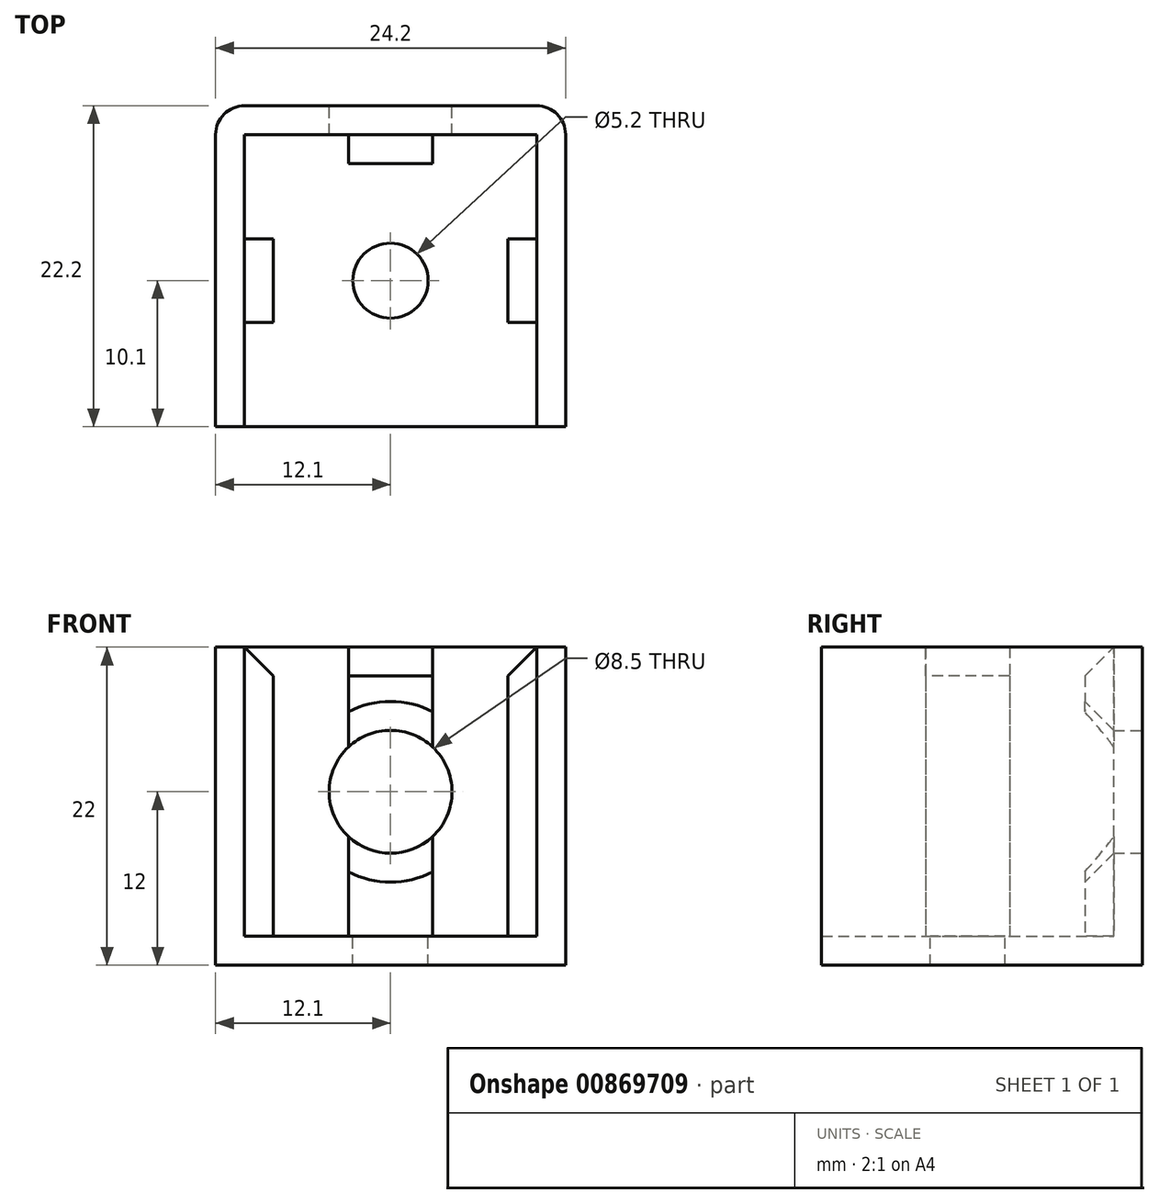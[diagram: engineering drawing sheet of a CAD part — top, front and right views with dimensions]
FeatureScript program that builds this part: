
annotation { "Feature Type Name" : "Feature", "Feature Type Description" : "" }
export const myFeature = defineFeature(function(context is Context, id is Id, definition is map)
    precondition{}
    {
        {
            var Q0;
            Q0=qCreatedBy(makeId("Top.planeOp"),FACE);
            var sketch = newSketch(context, id + "F0", { "sketchPlane" : qUnion([Q0])});
            skLineSegment(sketch, "E0.bottom", {"start": v(10.1, 10.1) * mm, "end": v(-10.1, 10.1) * mm});
            skLineSegment(sketch, "E0.top", {"start": v(10.1, -10.1) * mm, "end": v(-10.1, -10.1) * mm});
            skLineSegment(sketch, "E0.left", {"start": v(10.1, 10.1) * mm, "end": v(10.1, -10.1) * mm});
            skLineSegment(sketch, "E0.right", {"start": v(-10.1, 10.1) * mm, "end": v(-10.1, -10.1) * mm});
            skPoint(sketch, "E0.middle", {"position": v(0, 0) * mm});
            skSolve(sketch);
        }
        {
            var Q0;
            Q0=qCreatedBy(makeId("Top.planeOp"),FACE);
            var sketch = newSketch(context, id + "F1", { "sketchPlane" : qUnion([Q0])});
            skLineSegment(sketch, "E1.bottom", {"start": v(-12.1, 10.1) * mm, "end": v(12.1, 10.1) * mm});
            skLineSegment(sketch, "E1.top", {"start": v(-12.1, 12.1) * mm, "end": v(12.1, 12.1) * mm});
            skLineSegment(sketch, "E1.left", {"start": v(-12.1, 10.1) * mm, "end": v(-12.1, 12.1) * mm});
            skLineSegment(sketch, "E1.right", {"start": v(12.1, 10.1) * mm, "end": v(12.1, 12.1) * mm});
            skLineSegment(sketch, "E2.bottom", {"start": v(-2.9, 10.1) * mm, "end": v(2.9, 10.1) * mm});
            skLineSegment(sketch, "E2.top", {"start": v(-2.9, 8.1) * mm, "end": v(2.9, 8.1) * mm});
            skLineSegment(sketch, "E2.left", {"start": v(-2.9, 10.1) * mm, "end": v(-2.9, 8.1) * mm});
            skLineSegment(sketch, "E2.right", {"start": v(2.9, 10.1) * mm, "end": v(2.9, 8.1) * mm});
            skLineSegment(sketch, "E3", {"start": v(0, 0) * mm, "end": v(0, 8.1) * mm, "construction": true});
            skLineSegment(sketch, "E4", {"start": v(0, 8.1) * mm, "end": v(0, 10.1) * mm, "construction": true});
            skSolve(sketch);
        }
        {
            var Q0;
            Q0=qSketchRegion(id+"F1",true);
            extrude(context, id + "F2", {"entities" : qUnion([Q0]), "depth" : 20 * mm, "offsetDistance" : 25 * mm});
        }
        {
            var Q0;
            Q0=qCreatedBy(makeId("Front.planeOp"),FACE);
            var sketch = newSketch(context, id + "F3", { "sketchPlane" : qUnion([Q0])});
            skLineSegment(sketch, "E5", {"start": v(0, 0) * mm, "end": v(0, 26.41) * mm, "construction": true});
            skSolve(sketch);
        }
        {
            var Q0;
            Q0=makeQuery(id+"F2.opExtrude","SWEPT_BODY",BODY,{"disambiguationData":[OSD([sQuery(id+"F1.wireOp",EDGE,"E1.bottom"),sQuery(id+"F1.wireOp",EDGE,"E1.top"),sQuery(id+"F1.wireOp",EDGE,"E1.left"),sQuery(id+"F1.wireOp",EDGE,"E1.right"),sQuery(id+"F1.wireOp",EDGE,"E2.top"),sQuery(id+"F1.wireOp",EDGE,"E2.left"),sQuery(id+"F1.wireOp",EDGE,"E2.right")])]});
            var Q1;
            Q1=sQuery(id+"F3.wireOp",EDGE,"E5");
            circularPattern(context, id + "F4", {"operationType" : NewBodyOperationType.ADD, "entities" : qUnion([Q0]), "axis" : qUnion([Q1]), "angle" : 360 * degree, "instanceCount" : 4, "equalSpace" : true});
        }
        {
            var Q0;
            Q0=makeQuery(id+"F2.opExtrude","SWEPT_FACE",FACE,{"disambiguationData":[OSD([sQuery(id+"F1.wireOp",EDGE,"E1.top")])]});
            var sketch = newSketch(context, id + "F5", { "sketchPlane" : qUnion([Q0])});
            skCircle(sketch, "E6", {"center": v(0, 10) * mm, "radius": 4.25 * mm});
            skSolve(sketch);
        }
        {
            var Q0;
            Q0=qSketchRegion(id+"F5",true);
            extrude(context, id + "F6", {"entities" : qUnion([Q0]), "operationType" : NewBodyOperationType.REMOVE, "endBound" : BoundingType.THROUGH_ALL, "oppositeDirection" : true, "depth" : 25 * mm, "offsetDistance" : 25 * mm});
        }
        {
            var Q0;
            {var subQ0=makeQuery(id+"F2.opExtrude","CAP_FACE",FACE,{"disambiguationData":[OSD([sQuery(id+"F1.wireOp",EDGE,"E1.bottom"),sQuery(id+"F1.wireOp",EDGE,"E1.top"),sQuery(id+"F1.wireOp",EDGE,"E1.left"),sQuery(id+"F1.wireOp",EDGE,"E1.right"),sQuery(id+"F1.wireOp",EDGE,"E2.top"),sQuery(id+"F1.wireOp",EDGE,"E2.left"),sQuery(id+"F1.wireOp",EDGE,"E2.right")])],"isStart":false});Q0=makeQuery(id+"F4.boolean.opBoolean","MERGE",FACE,{"derivedFrom":[subQ0,makeQuery(id+"F4.opPattern","COPY",FACE,{"derivedFrom":subQ0,"instanceName":"1"}),makeQuery(id+"F4.opPattern","COPY",FACE,{"derivedFrom":subQ0,"instanceName":"2"}),makeQuery(id+"F4.opPattern","COPY",FACE,{"derivedFrom":subQ0,"instanceName":"3"})]});}
            var sketch = newSketch(context, id + "F7", { "sketchPlane" : qUnion([Q0])});
            skLineSegment(sketch, "E7", {"start": v(-10.1, -10.1) * mm, "end": v(-12.1, -10.1) * mm});
            skLineSegment(sketch, "E8", {"start": v(-12.1, -10.1) * mm, "end": v(-12.1, -12.1) * mm});
            skLineSegment(sketch, "E9", {"start": v(-12.1, -12.1) * mm, "end": v(12.1, -12.1) * mm});
            skLineSegment(sketch, "E10", {"start": v(12.1, -12.1) * mm, "end": v(12.1, -10.1) * mm});
            skLineSegment(sketch, "E11", {"start": v(12.1, -10.1) * mm, "end": v(10.1, -10.1) * mm});
            skLineSegment(sketch, "E12", {"start": v(10.1, -10.1) * mm, "end": v(2.9, -8.1) * mm});
            skLineSegment(sketch, "E13", {"start": v(2.9, -8.1) * mm, "end": v(-2.9, -8.1) * mm});
            skLineSegment(sketch, "E14", {"start": v(-2.9, -8.1) * mm, "end": v(-10.1, -10.1) * mm});
            skSolve(sketch);
        }
        {
            var Q0;
            Q0=qSketchRegion(id+"F7",true);
            extrude(context, id + "F8", {"entities" : qUnion([Q0]), "operationType" : NewBodyOperationType.REMOVE, "endBound" : BoundingType.THROUGH_ALL, "oppositeDirection" : true, "depth" : 25 * mm, "offsetDistance" : 25 * mm});
        }
        {
            var Q0;
            {var subQ0=makeQuery(id+"F2.opExtrude","CAP_FACE",FACE,{"disambiguationData":[OSD([sQuery(id+"F1.wireOp",EDGE,"E1.bottom"),sQuery(id+"F1.wireOp",EDGE,"E1.top"),sQuery(id+"F1.wireOp",EDGE,"E1.left"),sQuery(id+"F1.wireOp",EDGE,"E1.right"),sQuery(id+"F1.wireOp",EDGE,"E2.top"),sQuery(id+"F1.wireOp",EDGE,"E2.left"),sQuery(id+"F1.wireOp",EDGE,"E2.right")])],"isStart":true});Q0=makeQuery(id+"F4.boolean.opBoolean","MERGE",FACE,{"derivedFrom":[subQ0,makeQuery(id+"F4.opPattern","COPY",FACE,{"derivedFrom":subQ0,"instanceName":"1"}),makeQuery(id+"F4.opPattern","COPY",FACE,{"derivedFrom":subQ0,"instanceName":"2"}),makeQuery(id+"F4.opPattern","COPY",FACE,{"derivedFrom":subQ0,"instanceName":"3"})]});}
            var sketch = newSketch(context, id + "F9", { "sketchPlane" : qUnion([Q0])});
            skLineSegment(sketch, "E15.bottom", {"start": v(12.1, -12.1) * mm, "end": v(-12.1, -12.1) * mm});
            skLineSegment(sketch, "E15.top", {"start": v(12.1, 10.1) * mm, "end": v(-12.1, 10.1) * mm});
            skLineSegment(sketch, "E15.left", {"start": v(12.1, -12.1) * mm, "end": v(12.1, 10.1) * mm});
            skLineSegment(sketch, "E15.right", {"start": v(-12.1, -12.1) * mm, "end": v(-12.1, 10.1) * mm});
            skCircle(sketch, "E16", {"center": v(0, 0) * mm, "radius": 2.6 * mm});
            skSolve(sketch);
        }
        {
            var Q0;
            Q0=qSketchRegion(id+"F9",true);
            extrude(context, id + "F10", {"entities" : qUnion([Q0]), "operationType" : NewBodyOperationType.ADD, "depth" : 2 * mm, "offsetDistance" : 25 * mm});
        }
        {
            var Q0;
            Q0=makeQuery(id+"F2.opExtrude","SWEPT_EDGE",EDGE,{"disambiguationData":[OSD([sQuery(id+"F1.wireOp",EDGE,"E1.top"),sQuery(id+"F1.wireOp",EDGE,"E1.left")])]});
            var Q1;
            Q1=makeQuery(id+"F2.opExtrude","SWEPT_EDGE",EDGE,{"disambiguationData":[OSD([sQuery(id+"F1.wireOp",EDGE,"E1.top"),sQuery(id+"F1.wireOp",EDGE,"E1.right")])]});
            fillet(context, id + "F11", {"entities" : qUnion([Q0, Q1]), "radius" : 2 * mm, "tangentPropagation" : true, "allowEdgeOverflow" : false});
        }
        {
            var Q0;
            Q0=makeQuery(id+"F6.boolean.opBoolean","INTERSECT",EDGE,{"disambiguationData":[OD(1.0)],"derivedFrom":[makeQuery(id+"F2.opExtrude","SWEPT_FACE",FACE,{"disambiguationData":[OSD([sQuery(id+"F1.wireOp",EDGE,"E2.top")])]}),makeQuery(id+"F6.opExtrude","SWEPT_FACE",FACE,{"disambiguationData":[OSD([sQuery(id+"F5.wireOp",EDGE,"E6")])]})]});
            var Q1;
            Q1=makeQuery(id+"F6.boolean.opBoolean","INTERSECT",EDGE,{"disambiguationData":[OD(0.0)],"derivedFrom":[makeQuery(id+"F2.opExtrude","SWEPT_FACE",FACE,{"disambiguationData":[OSD([sQuery(id+"F1.wireOp",EDGE,"E2.top")])]}),makeQuery(id+"F6.opExtrude","SWEPT_FACE",FACE,{"disambiguationData":[OSD([sQuery(id+"F5.wireOp",EDGE,"E6")])]})]});
            var Q2;
            Q2=makeQuery(id+"F4.opPattern","COPY",EDGE,{"derivedFrom":makeQuery(id+"F2.opExtrude","CAP_EDGE",EDGE,{"disambiguationData":[OSD([sQuery(id+"F1.wireOp",EDGE,"E2.top")])],"isStart":false}),"instanceName":"1"});
            var Q3;
            Q3=makeQuery(id+"F2.opExtrude","CAP_EDGE",EDGE,{"disambiguationData":[OSD([sQuery(id+"F1.wireOp",EDGE,"E2.top")])],"isStart":false});
            var Q4;
            Q4=makeQuery(id+"F4.opPattern","COPY",EDGE,{"derivedFrom":makeQuery(id+"F2.opExtrude","CAP_EDGE",EDGE,{"disambiguationData":[OSD([sQuery(id+"F1.wireOp",EDGE,"E2.top")])],"isStart":false}),"instanceName":"3"});
            chamfer(context, id + "F12", {"entities" : qUnion([Q0, Q1, Q2, Q3, Q4]), "width" : 2 * mm, "tangentPropagation" : true});
        }
    });
